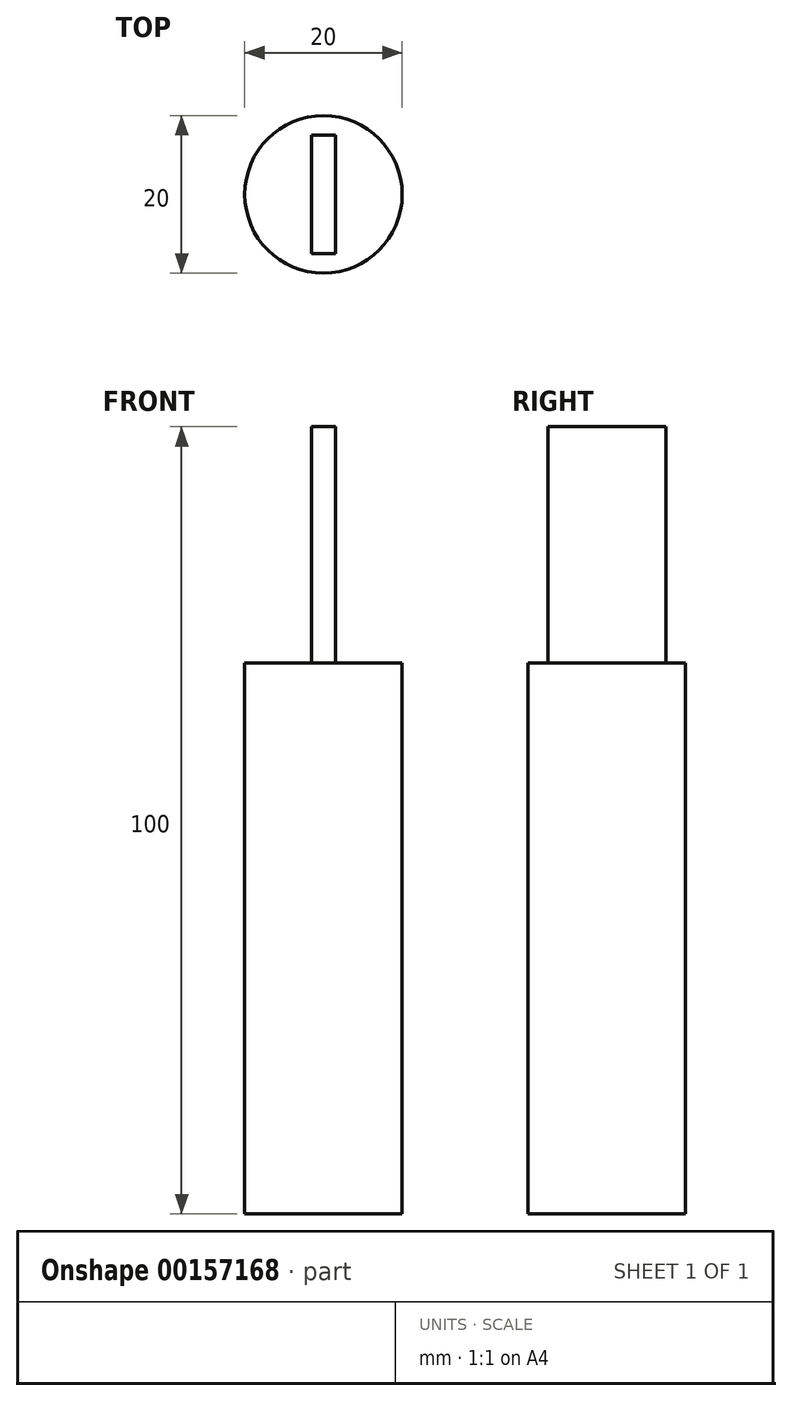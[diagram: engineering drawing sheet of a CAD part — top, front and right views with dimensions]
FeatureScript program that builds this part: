
annotation { "Feature Type Name" : "Feature", "Feature Type Description" : "" }
export const myFeature = defineFeature(function(context is Context, id is Id, definition is map)
    precondition{}
    {
        {
            var Q0;
            Q0=qCreatedBy(makeId("Top.planeOp"),FACE);
            var sketch = newSketch(context, id + "F2", { "sketchPlane" : qUnion([Q0])});
            skLineSegment(sketch, "E0.bottom", {"start": v(1.5, -7.5) * mm, "end": v(-1.5, -7.5) * mm});
            skLineSegment(sketch, "E0.top", {"start": v(1.5, 7.5) * mm, "end": v(-1.5, 7.5) * mm});
            skLineSegment(sketch, "E0.left", {"start": v(1.5, -7.5) * mm, "end": v(1.5, 7.5) * mm});
            skLineSegment(sketch, "E0.right", {"start": v(-1.5, -7.5) * mm, "end": v(-1.5, 7.5) * mm});
            skPoint(sketch, "E0.middle", {"position": v(0, 0) * mm});
            skCircle(sketch, "E1", {"center": v(0, 0) * mm, "radius": 10 * mm});
            skSolve(sketch);
        }
        {
            var Q0;
            Q0=makeQuery(id+"F2.imprint","IMPRINT",FACE,{"disambiguationData":[TD([[makeQuery(id+"F2.imprint","IMPRINT",EDGE,{"derivedFrom":sQuery(id+"F2.wireOp",EDGE,"E0.bottom")}),-1.0]])]});
            extrude(context, id + "F0", {"entities" : qUnion([Q0]), "depth" : 100 * mm});
        }
        {
            var Q0;
            Q0=makeQuery(id+"F2.imprint","IMPRINT",FACE,{"disambiguationData":[TD([[makeQuery(id+"F2.imprint","IMPRINT",EDGE,{"derivedFrom":sQuery(id+"F2.wireOp",EDGE,"E0.bottom")}),1.0]])]});
            extrude(context, id + "F1", {"entities" : qUnion([Q0]), "operationType" : NewBodyOperationType.ADD, "depth" : 70 * mm});
        }
    });
